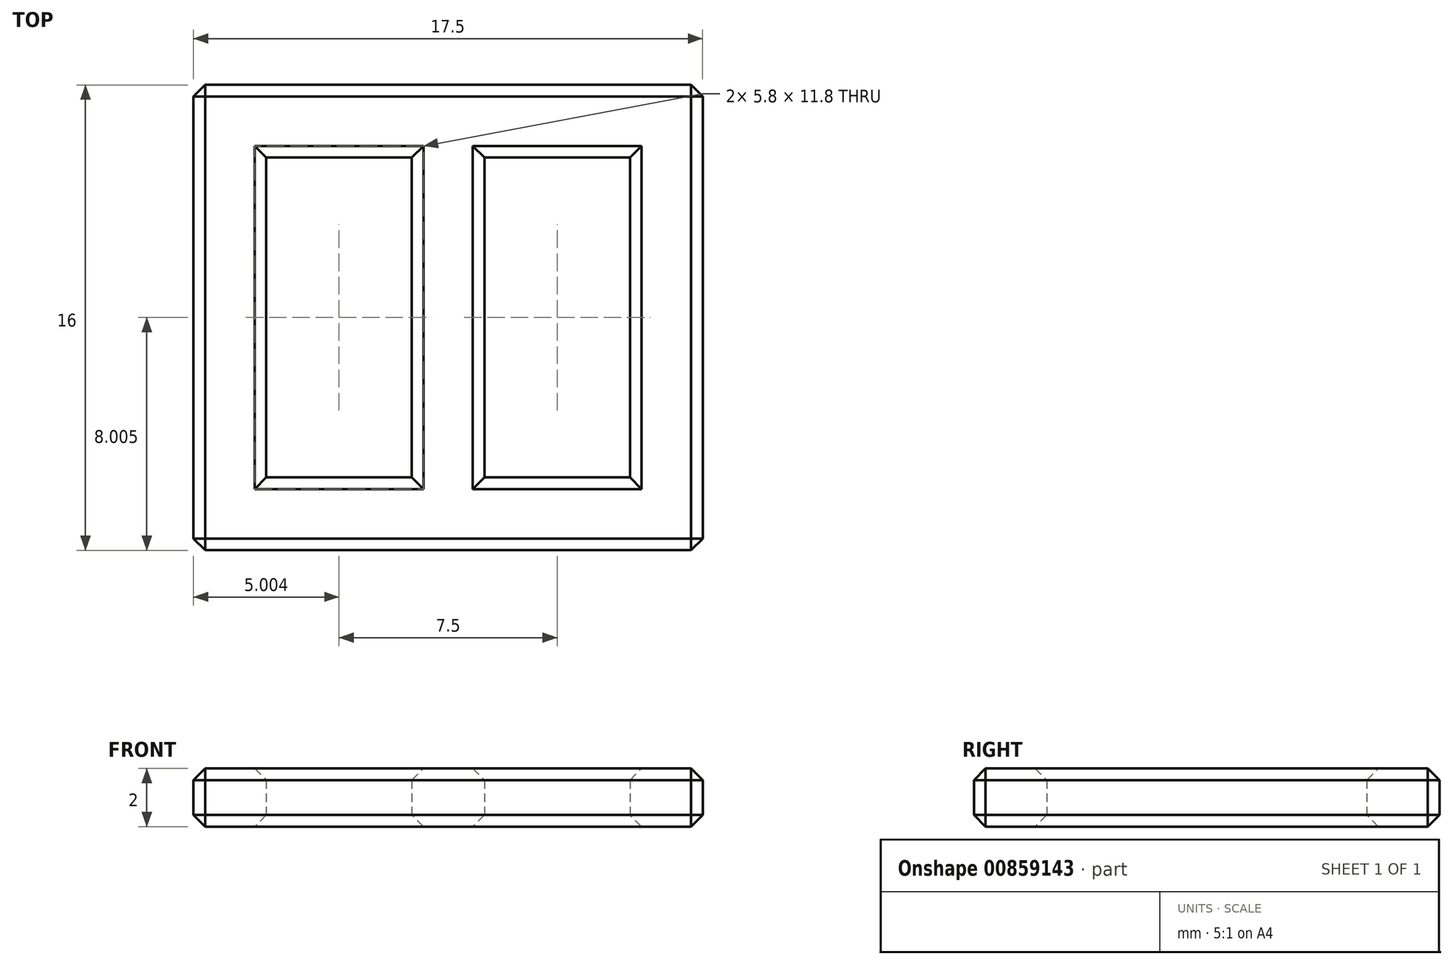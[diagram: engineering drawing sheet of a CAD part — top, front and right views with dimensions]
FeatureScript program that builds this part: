
annotation { "Feature Type Name" : "Feature", "Feature Type Description" : "" }
export const myFeature = defineFeature(function(context is Context, id is Id, definition is map)
    precondition{}
    {
        {
            var Q0;
            Q0=qCreatedBy(makeId("Top.planeOp"),FACE);
            var sketch = newSketch(context, id + "F0", { "sketchPlane" : qUnion([Q0])});
            skLineSegment(sketch, "E0", {"start": v(-3.9, 12.11) * mm, "end": v(-3.9, -3.89) * mm});
            skLineSegment(sketch, "E1", {"start": v(-3.9, -3.89) * mm, "end": v(13.6, -3.89) * mm});
            skLineSegment(sketch, "E2", {"start": v(13.6, -3.89) * mm, "end": v(13.6, 12.11) * mm});
            skLineSegment(sketch, "E3", {"start": v(13.6, 12.11) * mm, "end": v(-3.9, 12.11) * mm});
            skLineSegment(sketch, "E4.bottom", {"start": v(-1.4, 9.61) * mm, "end": v(3.6, 9.61) * mm});
            skLineSegment(sketch, "E4.top", {"start": v(-1.4, -1.39) * mm, "end": v(3.6, -1.39) * mm});
            skLineSegment(sketch, "E4.left", {"start": v(-1.4, 9.61) * mm, "end": v(-1.4, -1.39) * mm});
            skLineSegment(sketch, "E4.right", {"start": v(3.6, 9.61) * mm, "end": v(3.6, -1.39) * mm});
            skPoint(sketch, "E5.firstSnap0", {"position": v(1.1, 9.61) * mm});
            skLineSegment(sketch, "E5.bottom", {"start": v(6.1, 9.61) * mm, "end": v(11.1, 9.61) * mm});
            skLineSegment(sketch, "E5.top", {"start": v(6.1, -1.39) * mm, "end": v(11.1, -1.39) * mm});
            skLineSegment(sketch, "E5.left", {"start": v(6.1, 9.61) * mm, "end": v(6.1, -1.39) * mm});
            skLineSegment(sketch, "E5.right", {"start": v(11.1, 9.61) * mm, "end": v(11.1, -1.39) * mm});
            skSolve(sketch);
        }
        {
            var Q0;
            Q0=qSketchRegion(id+"F0",true);
            extrude(context, id + "F1", {"entities" : qUnion([Q0]), "depth" : 2 * mm, "offsetDistance" : 25 * mm});
        }
        {
            var Q0;
            Q0=makeQuery(id+"F1.opExtrude","CAP_EDGE",EDGE,{"disambiguationData":[OSD([sQuery(id+"F0.wireOp",EDGE,"E1")])],"isStart":false});
            var Q1;
            Q1=makeQuery(id+"F1.opExtrude","CAP_EDGE",EDGE,{"disambiguationData":[OSD([sQuery(id+"F0.wireOp",EDGE,"E0")])],"isStart":false});
            var Q2;
            Q2=makeQuery(id+"F1.opExtrude","CAP_EDGE",EDGE,{"disambiguationData":[OSD([sQuery(id+"F0.wireOp",EDGE,"E4.left")])],"isStart":false});
            var Q3;
            Q3=makeQuery(id+"F1.opExtrude","CAP_EDGE",EDGE,{"disambiguationData":[OSD([sQuery(id+"F0.wireOp",EDGE,"E4.right")])],"isStart":false});
            var Q4;
            Q4=makeQuery(id+"F1.opExtrude","CAP_EDGE",EDGE,{"disambiguationData":[OSD([sQuery(id+"F0.wireOp",EDGE,"E5.left")])],"isStart":false});
            var Q5;
            Q5=makeQuery(id+"F1.opExtrude","CAP_EDGE",EDGE,{"disambiguationData":[OSD([sQuery(id+"F0.wireOp",EDGE,"E5.right")])],"isStart":false});
            var Q6;
            Q6=makeQuery(id+"F1.opExtrude","CAP_EDGE",EDGE,{"disambiguationData":[OSD([sQuery(id+"F0.wireOp",EDGE,"E4.bottom")])],"isStart":false});
            var Q7;
            Q7=makeQuery(id+"F1.opExtrude","CAP_EDGE",EDGE,{"disambiguationData":[OSD([sQuery(id+"F0.wireOp",EDGE,"E4.top")])],"isStart":false});
            var Q8;
            Q8=makeQuery(id+"F1.opExtrude","CAP_EDGE",EDGE,{"disambiguationData":[OSD([sQuery(id+"F0.wireOp",EDGE,"E5.top")])],"isStart":false});
            var Q9;
            Q9=makeQuery(id+"F1.opExtrude","CAP_EDGE",EDGE,{"disambiguationData":[OSD([sQuery(id+"F0.wireOp",EDGE,"E2")])],"isStart":false});
            var Q10;
            Q10=makeQuery(id+"F1.opExtrude","CAP_EDGE",EDGE,{"disambiguationData":[OSD([sQuery(id+"F0.wireOp",EDGE,"E3")])],"isStart":false});
            var Q11;
            Q11=makeQuery(id+"F1.opExtrude","CAP_EDGE",EDGE,{"disambiguationData":[OSD([sQuery(id+"F0.wireOp",EDGE,"E5.bottom")])],"isStart":false});
            var Q12;
            Q12=makeQuery(id+"F1.opExtrude","SWEPT_EDGE",EDGE,{"disambiguationData":[OSD([sQuery(id+"F0.wireOp",EDGE,"E2"),sQuery(id+"F0.wireOp",EDGE,"E3")])]});
            var Q13;
            Q13=makeQuery(id+"F1.opExtrude","SWEPT_EDGE",EDGE,{"disambiguationData":[OSD([sQuery(id+"F0.wireOp",EDGE,"E0"),sQuery(id+"F0.wireOp",EDGE,"E3")])]});
            var Q14;
            Q14=makeQuery(id+"F1.opExtrude","SWEPT_EDGE",EDGE,{"disambiguationData":[OSD([sQuery(id+"F0.wireOp",EDGE,"E1"),sQuery(id+"F0.wireOp",EDGE,"E2")])]});
            var Q15;
            Q15=makeQuery(id+"F1.opExtrude","SWEPT_EDGE",EDGE,{"disambiguationData":[OSD([sQuery(id+"F0.wireOp",EDGE,"E0"),sQuery(id+"F0.wireOp",EDGE,"E1")])]});
            var Q16;
            Q16=makeQuery(id+"F1.opExtrude","CAP_EDGE",EDGE,{"disambiguationData":[OSD([sQuery(id+"F0.wireOp",EDGE,"E1")])],"isStart":true});
            var Q17;
            Q17=makeQuery(id+"F1.opExtrude","CAP_EDGE",EDGE,{"disambiguationData":[OSD([sQuery(id+"F0.wireOp",EDGE,"E2")])],"isStart":true});
            var Q18;
            Q18=makeQuery(id+"F1.opExtrude","CAP_EDGE",EDGE,{"disambiguationData":[OSD([sQuery(id+"F0.wireOp",EDGE,"E5.right")])],"isStart":true});
            var Q19;
            Q19=makeQuery(id+"F1.opExtrude","CAP_EDGE",EDGE,{"disambiguationData":[OSD([sQuery(id+"F0.wireOp",EDGE,"E5.bottom")])],"isStart":true});
            var Q20;
            Q20=makeQuery(id+"F1.opExtrude","CAP_EDGE",EDGE,{"disambiguationData":[OSD([sQuery(id+"F0.wireOp",EDGE,"E5.left")])],"isStart":true});
            var Q21;
            Q21=makeQuery(id+"F1.opExtrude","CAP_EDGE",EDGE,{"disambiguationData":[OSD([sQuery(id+"F0.wireOp",EDGE,"E5.top")])],"isStart":true});
            var Q22;
            Q22=makeQuery(id+"F1.opExtrude","CAP_EDGE",EDGE,{"disambiguationData":[OSD([sQuery(id+"F0.wireOp",EDGE,"E4.right")])],"isStart":true});
            var Q23;
            Q23=makeQuery(id+"F1.opExtrude","CAP_EDGE",EDGE,{"disambiguationData":[OSD([sQuery(id+"F0.wireOp",EDGE,"E4.bottom")])],"isStart":true});
            var Q24;
            Q24=makeQuery(id+"F1.opExtrude","CAP_EDGE",EDGE,{"disambiguationData":[OSD([sQuery(id+"F0.wireOp",EDGE,"E4.top")])],"isStart":true});
            var Q25;
            Q25=makeQuery(id+"F1.opExtrude","CAP_EDGE",EDGE,{"disambiguationData":[OSD([sQuery(id+"F0.wireOp",EDGE,"E4.left")])],"isStart":true});
            var Q26;
            Q26=makeQuery(id+"F1.opExtrude","CAP_EDGE",EDGE,{"disambiguationData":[OSD([sQuery(id+"F0.wireOp",EDGE,"E0")])],"isStart":true});
            var Q27;
            Q27=makeQuery(id+"F1.opExtrude","CAP_EDGE",EDGE,{"disambiguationData":[OSD([sQuery(id+"F0.wireOp",EDGE,"E3")])],"isStart":true});
            chamfer(context, id + "F2", {"entities" : qUnion([Q0, Q1, Q2, Q3, Q4, Q5, Q6, Q7, Q8, Q9, Q10, Q11, Q12, Q13, Q14, Q15, Q16, Q17, Q18, Q19, Q20, Q21, Q22, Q23, Q24, Q25, Q26, Q27]), "width" : .4 * mm, "tangentPropagation" : true});
        }
    });
